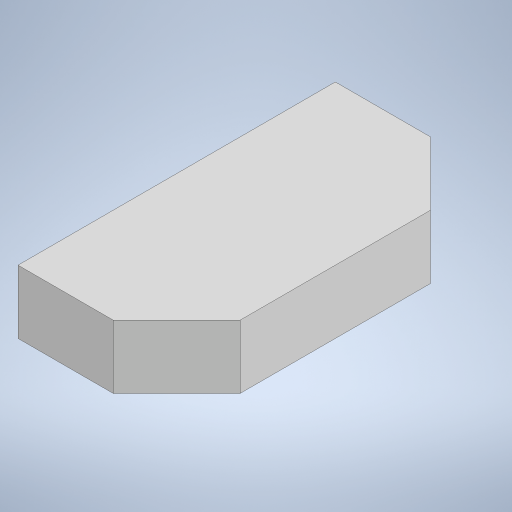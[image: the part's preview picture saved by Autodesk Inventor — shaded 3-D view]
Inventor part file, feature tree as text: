
AUTODESK INVENTOR PART (.ipt)
format: ipt  version: 2023 (Build 270158000, 158)  size: 216,576 bytes
history: native  units: mm
features: extrude x3, sketch x3, other x1, chamfer x1
ambient origin geometry x8: Origin, YZ Plane, XZ Plane, XY Plane, X Axis, Y Axis, Z Axis, Center Point
bodies: Body1 (feature_tree)
feature tree (8):
  other  "솔리드1"
  extrude  "돌출1"  Depth=50.0mm
  chamfer  "모따기1"  Distance=25.0mm
  extrude  "돌출2"  Depth=10.0mm TaperAngle=0.0deg
  extrude  "돌출3"  Depth=10.0mm TaperAngle=45.0deg
  sketch  "스케치1"
  sketch  "스케치2"
  sketch  "스케치3"
